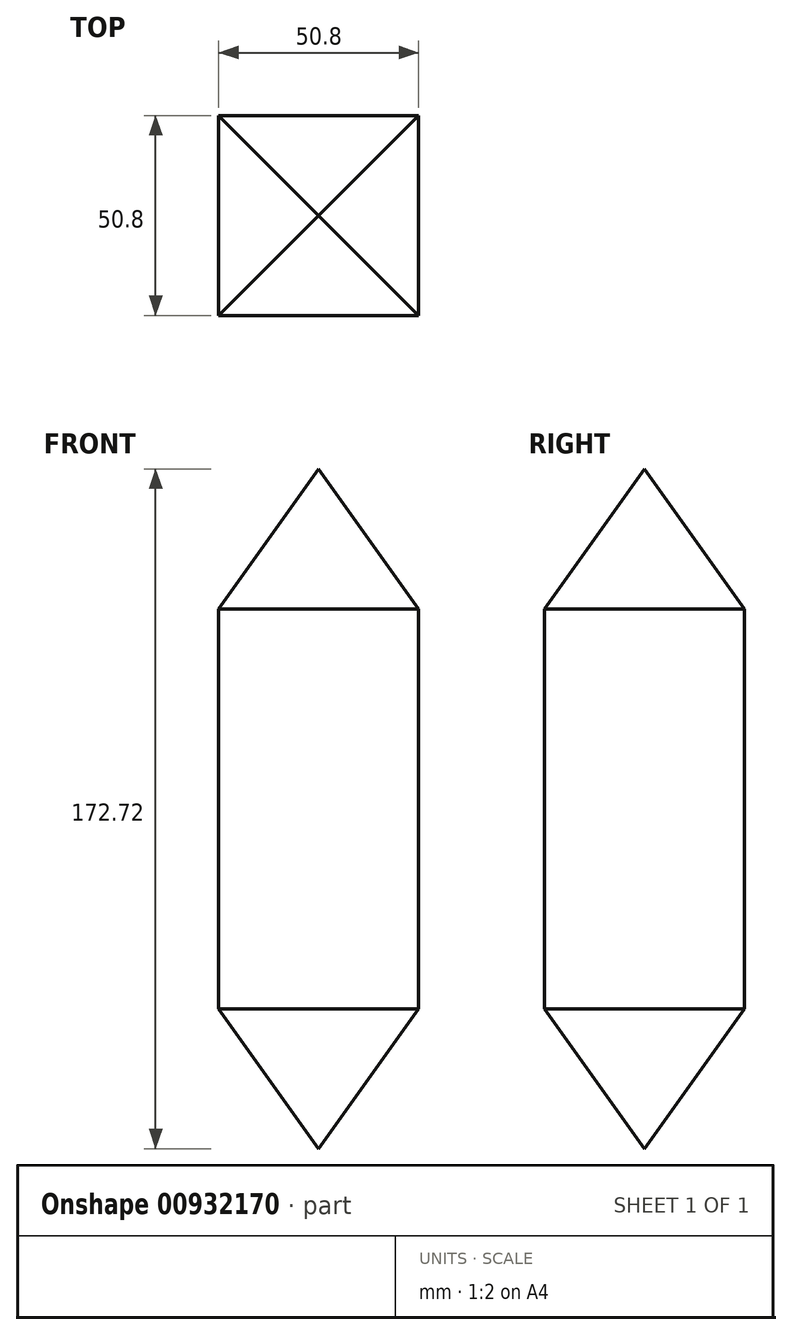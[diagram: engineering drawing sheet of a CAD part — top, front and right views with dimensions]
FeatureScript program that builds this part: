
annotation { "Feature Type Name" : "Feature", "Feature Type Description" : "" }
export const myFeature = defineFeature(function(context is Context, id is Id, definition is map)
    precondition{}
    {
        {
            var Q0;
            Q0=qCreatedBy(makeId("Right.planeOp"),FACE);
            var sketch = newSketch(context, id + "F0", { "sketchPlane" : qUnion([Q0])});
            skLineSegment(sketch, "E0.bottom", {"start": v(-25.4, 50.8) * mm, "end": v(25.4, 50.8) * mm});
            skLineSegment(sketch, "E0.top", {"start": v(-25.4, -50.8) * mm, "end": v(25.4, -50.8) * mm});
            skLineSegment(sketch, "E0.left", {"start": v(-25.4, 50.8) * mm, "end": v(-25.4, -50.8) * mm});
            skLineSegment(sketch, "E0.right", {"start": v(25.4, 50.8) * mm, "end": v(25.4, -50.8) * mm});
            skPoint(sketch, "E0.middle", {"position": v(0, 0) * mm});
            skLineSegment(sketch, "E1", {"start": v(-25.4, 50.8) * mm, "end": v(0, 86.36) * mm});
            skLineSegment(sketch, "E2", {"start": v(0, 86.36) * mm, "end": v(25.4, 50.8) * mm});
            skLineSegment(sketch, "E3", {"start": v(25.4, -50.8) * mm, "end": v(0, -86.36) * mm});
            skLineSegment(sketch, "E4", {"start": v(0, -86.36) * mm, "end": v(-25.4, -50.8) * mm});
            skSolve(sketch);
        }
        {
            var Q0;
            Q0 = qSketchRegion(id + "F0", true);
            extrude(context, id + "F1", {"entities" : qUnion([Q0]), "depth" : 50.8 * mm, "offsetDistance" : 25.4 * mm});
        }
        {
            var Q0;
            Q0=makeQuery(id+"F1.opExtrude","SWEPT_FACE",FACE,{"disambiguationData":[OSD([sQuery(id+"F0.wireOp",EDGE,"E0.right")])]});
            var sketch = newSketch(context, id + "F2", { "sketchPlane" : qUnion([Q0])});
            skLineSegment(sketch, "E5.bottom", {"start": v(-50.8, 50.8) * mm, "end": v(0, 50.8) * mm});
            skLineSegment(sketch, "E5.top", {"start": v(-50.8, 86.36) * mm, "end": v(0, 86.36) * mm});
            skLineSegment(sketch, "E5.left", {"start": v(-50.8, 50.8) * mm, "end": v(-50.8, 86.36) * mm});
            skLineSegment(sketch, "E5.right", {"start": v(0, 50.8) * mm, "end": v(0, 86.36) * mm});
            skLineSegment(sketch, "E6", {"start": v(-50.8, 50.8) * mm, "end": v(-25.4, 86.36) * mm});
            skLineSegment(sketch, "E7", {"start": v(-25.4, 86.36) * mm, "end": v(0, 50.8) * mm});
            skSolve(sketch);
        }
        {
            var Q0;
            {var subQ0=sQuery(id+"F2.wireOp",EDGE,"E5.left");Q0=makeQuery(id+"F2.imprint","IMPRINT",FACE,{"disambiguationData":[TD([[makeQuery(id+"F2.imprint","IMPRINT",EDGE,{"derivedFrom":subQ0}),-1.0]])]});}
            var Q1;
            {var subQ0=sQuery(id+"F2.wireOp",EDGE,"E5.right");Q1=makeQuery(id+"F2.imprint","IMPRINT",FACE,{"disambiguationData":[TD([[makeQuery(id+"F2.imprint","IMPRINT",EDGE,{"derivedFrom":subQ0}),1.0]])]});}
            extrude(context, id + "F3", {"entities" : qUnion([Q0, Q1]), "operationType" : NewBodyOperationType.REMOVE, "oppositeDirection" : true, "depth" : 50.8 * mm, "offsetDistance" : 25.4 * mm});
        }
        {
            var Q0;
            Q0=makeQuery(id+"F1.opExtrude","SWEPT_FACE",FACE,{"disambiguationData":[OSD([sQuery(id+"F0.wireOp",EDGE,"E0.right")])]});
            var sketch = newSketch(context, id + "F4", { "sketchPlane" : qUnion([Q0])});
            skLineSegment(sketch, "E8.bottom", {"start": v(-50.8, -50.8) * mm, "end": v(0, -50.8) * mm});
            skLineSegment(sketch, "E8.top", {"start": v(-50.8, -86.36) * mm, "end": v(0, -86.36) * mm});
            skLineSegment(sketch, "E8.left", {"start": v(-50.8, -50.8) * mm, "end": v(-50.8, -86.36) * mm});
            skLineSegment(sketch, "E8.right", {"start": v(0, -50.8) * mm, "end": v(0, -86.36) * mm});
            skLineSegment(sketch, "E9", {"start": v(-50.8, -50.8) * mm, "end": v(-25.4, -86.36) * mm});
            skLineSegment(sketch, "E10", {"start": v(-25.4, -86.36) * mm, "end": v(0, -50.8) * mm});
            skSolve(sketch);
        }
        {
            var Q0;
            {var subQ0=sQuery(id+"F4.wireOp",EDGE,"E8.right");Q0=makeQuery(id+"F4.imprint","IMPRINT",FACE,{"disambiguationData":[TD([[makeQuery(id+"F4.imprint","IMPRINT",EDGE,{"derivedFrom":subQ0}),-1.0]])]});}
            var Q1;
            {var subQ0=sQuery(id+"F4.wireOp",EDGE,"E8.left");Q1=makeQuery(id+"F4.imprint","IMPRINT",FACE,{"disambiguationData":[TD([[makeQuery(id+"F4.imprint","IMPRINT",EDGE,{"derivedFrom":subQ0}),1.0]])]});}
            extrude(context, id + "F5", {"entities" : qUnion([Q0, Q1]), "operationType" : NewBodyOperationType.REMOVE, "oppositeDirection" : true, "depth" : 50.8 * mm, "offsetDistance" : 25.4 * mm});
        }
    });
